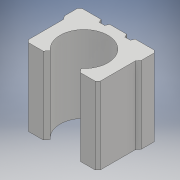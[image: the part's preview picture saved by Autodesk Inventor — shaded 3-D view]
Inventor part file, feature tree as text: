
AUTODESK INVENTOR PART (.ipt)
format: ipt  version: 2018 (Build 220112000, 112)  size: 178,688 bytes
history: native  units: mm
features: sketch x2, other x1, extrude x1, chamfer x1, hole x1
ambient origin geometry x8: Origin, YZ Plane, XZ Plane, XY Plane, X Axis, Y Axis, Z Axis, Center Point
bodies: Body1 (feature_tree)
feature tree (6):
  other  "Sólido1"
  extrude  "Extrusão1"  Depth=14.0mm
  chamfer  "Chanfro1"  Distance=9.0mm
  hole  "Furo1"  [1 undecoded]
  sketch  "Esboço1"  dims[d2=14.0mm d3=14.0mm]
  sketch  "Esboço2"  dims[d4=20.0mm d5=9.0mm d7=1.5mm d8=1.5mm d9=6.981317mm d10=6.981317mm d11=5.0mm d12=5.0mm d13=10.0mm d14=10.0mm d15=2.0mm d16=2.0mm d17=28.0mm d18=14.0mm d21=20.071286mm d22=20.071286mm d23=20.071286mm d24=20.071286mm d25=45.0mm d26=0.0mm d27=1.5mm d28=2.0mm d29=45.0deg d31=2.0mm d32=2.0mm d33=2.0mm d34=2.0mm d35=16.0mm d36=16.0mm d37=16.0mm d38=16.0mm d39=15.0mm d40=15.0mm d41=15.0mm d42=15.0mm d43=4.134mm d44=10.0mm d45=4.0mm d46=2.0mm d47=90.0deg d48=8.0mm d49=20.594885mm]
note: 1 required parameter value undecoded (feature->parameter linkage not recoverable at this tier; creation-order binding heuristic only, values carry confidence <= 0.55)
